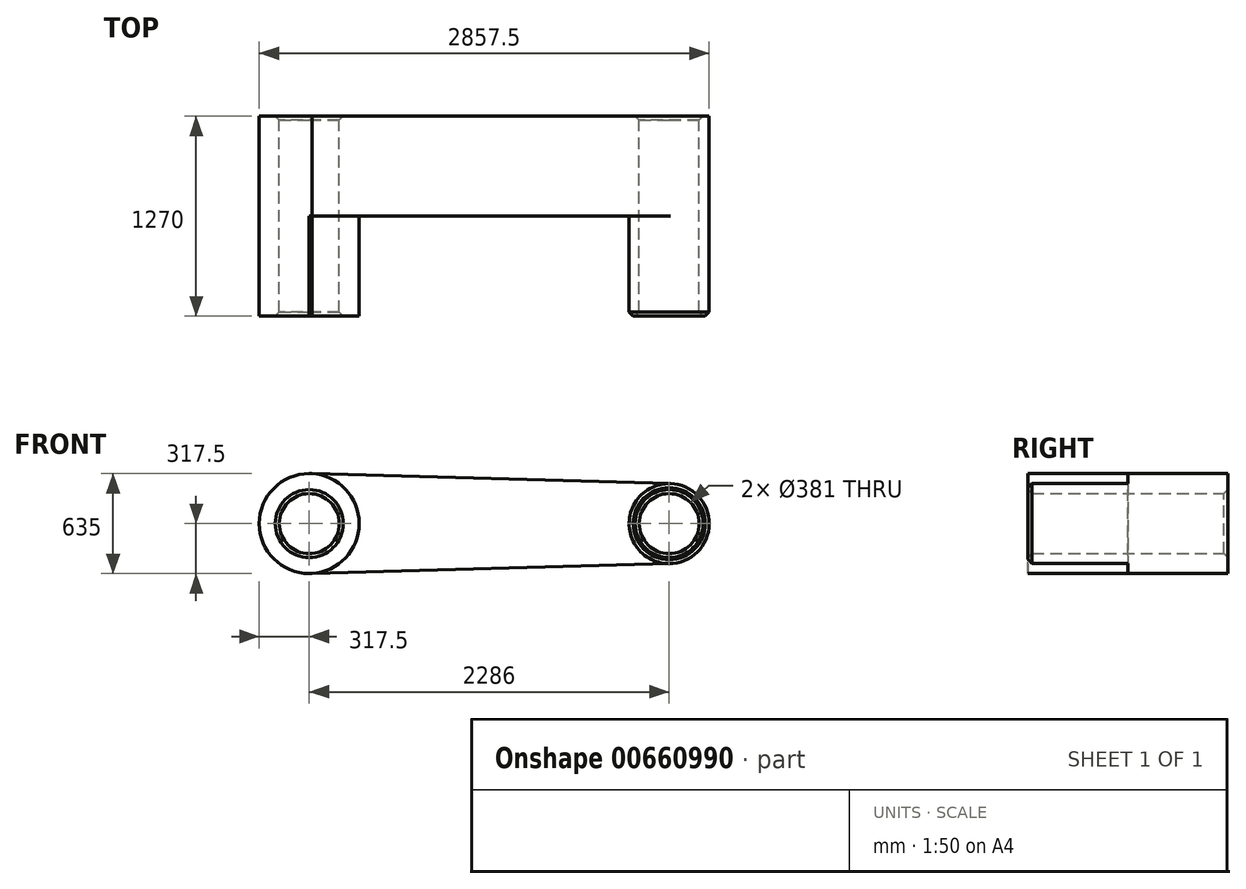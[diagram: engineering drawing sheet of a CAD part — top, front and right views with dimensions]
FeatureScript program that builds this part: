
annotation { "Feature Type Name" : "Feature", "Feature Type Description" : "" }
export const myFeature = defineFeature(function(context is Context, id is Id, definition is map)
    precondition{}
    {
        {
            var Q0;
            Q0=qCreatedBy(makeId("Front.planeOp"),FACE);
            var sketch = newSketch(context, id + "F0", { "sketchPlane" : qUnion([Q0])});
            skCircle(sketch, "E0", {"center": v(0, 0) * mm, "radius": 317.5 * mm});
            skCircle(sketch, "E1", {"center": v(2286, 0) * mm, "radius": 254 * mm});
            skLineSegment(sketch, "E2", {"start": v(0, -317.5) * mm, "end": v(2293.04, -253.9) * mm});
            skLineSegment(sketch, "E3", {"start": v(0, 317.5) * mm, "end": v(2293.04, 253.9) * mm});
            skCircle(sketch, "E4", {"center": v(0, 0) * mm, "radius": 190.5 * mm});
            skCircle(sketch, "E5", {"center": v(2286, 0) * mm, "radius": 190.5 * mm});
            skSolve(sketch);
        }
        {
            var Q0;
            Q0 = qSketchRegion(id + "F0", true);
            extrude(context, id + "F1", {"entities" : qUnion([Q0]), "depth" : 635 * mm, "offsetDistance" : 25.4 * mm});
        }
        {
            var Q0;
            Q0=makeQuery(id+"F0.imprint","IMPRINT",FACE,{"disambiguationData":[TD([[makeQuery(id+"F0.imprint","IMPRINT",EDGE,{"derivedFrom":sQuery(id+"F0.wireOp",EDGE,"E4")}),-1.0]])]});
            var Q1;
            Q1=makeQuery(id+"F0.imprint","IMPRINT",FACE,{"disambiguationData":[TD([[makeQuery(id+"F0.imprint","IMPRINT",EDGE,{"derivedFrom":sQuery(id+"F0.wireOp",EDGE,"E5")}),-1.0]])]});
            extrude(context, id + "F2", {"entities" : qUnion([Q0, Q1]), "operationType" : NewBodyOperationType.ADD, "depth" : 1270 * mm, "offsetDistance" : 25.4 * mm});
        }
        {
            var Q0;
            Q0=makeQuery(id+"F2.opExtrude","CAP_EDGE",EDGE,{"disambiguationData":[OSD([sQuery(id+"F0.wireOp",EDGE,"E4")])],"isStart":false});
            var Q1;
            Q1=makeQuery(id+"F1.opExtrude","CAP_EDGE",EDGE,{"disambiguationData":[OSD([sQuery(id+"F0.wireOp",EDGE,"E5")])],"isStart":true});
            var Q2;
            Q2=makeQuery(id+"F2.opExtrude","CAP_EDGE",EDGE,{"disambiguationData":[OSD([sQuery(id+"F0.wireOp",EDGE,"E5")])],"isStart":false});
            var Q3;
            {var subQ0=sQuery(id+"F0.wireOp",EDGE,"E0");Q3=makeQuery(id+"F2.opExtrude","CAP_EDGE",EDGE,{"disambiguationData":[OSD([subQ0]),TDD([makeQuery(id+"F0.imprint","IMPRINT",EDGE,{"disambiguationData":[TD([[makeQuery(id+"F0.imprint","INTERSECT",VERTEX,{"disambiguationData":[OD(1.0)],"derivedFrom":[subQ0,sQuery(id+"F0.wireOp",EDGE,"E3")]}),1.0]])],"derivedFrom":subQ0})])],"isStart":false});}
            var Q4;
            {var subQ0=sQuery(id+"F0.wireOp",EDGE,"E0");Q4=makeQuery(id+"F2.opExtrude","CAP_EDGE",EDGE,{"disambiguationData":[OSD([subQ0]),TDD([makeQuery(id+"F0.imprint","IMPRINT",EDGE,{"disambiguationData":[TD([[makeQuery(id+"F0.imprint","INTERSECT",VERTEX,{"disambiguationData":[OD(0.0)],"derivedFrom":[subQ0,sQuery(id+"F0.wireOp",EDGE,"E2")]}),1.0]])],"derivedFrom":subQ0})])],"isStart":false});}
            var Q5;
            Q5=makeQuery(id+"F2.opExtrude","CAP_EDGE",EDGE,{"disambiguationData":[OSD([sQuery(id+"F0.wireOp",EDGE,"E1")])],"isStart":false});
            var Q6;
            Q6=makeQuery(id+"F1.opExtrude","CAP_EDGE",EDGE,{"disambiguationData":[OSD([sQuery(id+"F0.wireOp",EDGE,"E4")])],"isStart":true});
            chamfer(context, id + "F3", {"entities" : qUnion([Q0, Q1, Q2, Q3, Q4, Q5, Q6]), "width" : 25.4 * mm, "tangentPropagation" : true});
        }
    });
